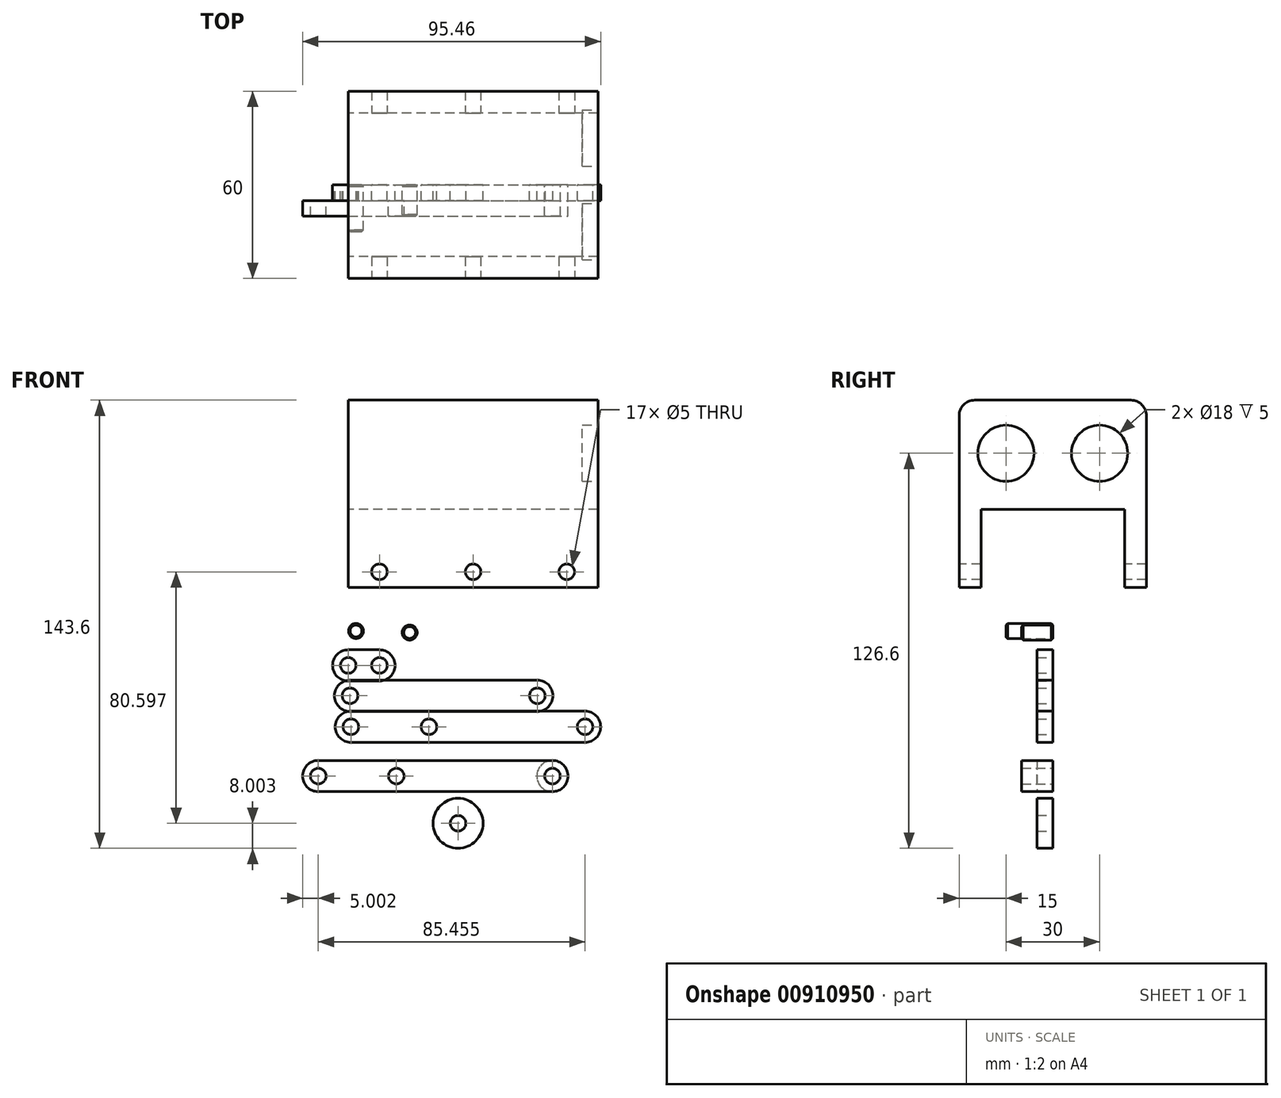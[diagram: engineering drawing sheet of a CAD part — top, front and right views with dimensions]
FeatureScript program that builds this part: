
annotation { "Feature Type Name" : "Feature", "Feature Type Description" : "" }
export const myFeature = defineFeature(function(context is Context, id is Id, definition is map)
    precondition{}
    {
        {
            assignVariable(context, id + "F0", {"name" : "thickness", "anyValue" : 5});
        }
        {
            var Q0;
            Q0=qCreatedBy(makeId("Front.planeOp"),FACE);
            var sketch = newSketch(context, id + "F1", { "sketchPlane" : qUnion([Q0])});
            skArc(sketch, "E0", {"start": v(0, 5) * mm, "mid": v(-5, 0) * mm, "end": v(0, -5) * mm});
            skArc(sketch, "E1", {"start": v(10, -5) * mm, "mid": v(15, 0) * mm, "end": v(10, 5) * mm});
            skLineSegment(sketch, "E2", {"start": v(0, 5) * mm, "end": v(10, 5) * mm});
            skLineSegment(sketch, "E3", {"start": v(0, -5) * mm, "end": v(10, -5) * mm});
            skCircle(sketch, "E4", {"center": v(0, 0) * mm, "radius": 2.5 * mm});
            skCircle(sketch, "E5", {"center": v(10, 0) * mm, "radius": 2.5 * mm});
            skSolve(sketch);
        }
        {
            var Q0;
            Q0=makeQuery(id+"F1.imprint","IMPRINT",FACE,{"disambiguationData":[TD([[makeQuery(id+"F1.imprint","IMPRINT",EDGE,{"derivedFrom":sQuery(id+"F1.wireOp",EDGE,"E0")}),1.0]])]});
            extrude(context, id + "F2", {"entities" : qUnion([Q0]), "depth" : (getVariable(context, 'thickness')) * mm, "offsetDistance" : 25 * mm});
        }
        {
            var Q0;
            Q0=qCreatedBy(makeId("Front.planeOp"),FACE);
            var sketch = newSketch(context, id + "F3", { "sketchPlane" : qUnion([Q0])});
            skArc(sketch, "E6", {"start": v(0.57, -4.73) * mm, "mid": v(-4.43, -9.73) * mm, "end": v(0.57, -14.73) * mm});
            skArc(sketch, "E7", {"start": v(60.57, -14.73) * mm, "mid": v(65.57, -9.73) * mm, "end": v(60.57, -4.73) * mm});
            skLineSegment(sketch, "E8", {"start": v(0.57, -4.73) * mm, "end": v(60.57, -4.73) * mm});
            skLineSegment(sketch, "E9", {"start": v(0.57, -14.73) * mm, "end": v(60.57, -14.73) * mm});
            skCircle(sketch, "E10", {"center": v(0.57, -9.73) * mm, "radius": 2.5 * mm});
            skCircle(sketch, "E11", {"center": v(60.57, -9.73) * mm, "radius": 2.5 * mm});
            skSolve(sketch);
        }
        {
            var Q0;
            Q0=makeQuery(id+"F3.imprint","IMPRINT",FACE,{"disambiguationData":[TD([[makeQuery(id+"F3.imprint","IMPRINT",EDGE,{"derivedFrom":sQuery(id+"F3.wireOp",EDGE,"E6")}),1.0]])]});
            extrude(context, id + "F4", {"entities" : qUnion([Q0]), "depth" : (getVariable(context, 'thickness')) * mm, "offsetDistance" : 25 * mm});
        }
        {
            var Q0;
            Q0=qCreatedBy(makeId("Front.planeOp"),FACE);
            var sketch = newSketch(context, id + "F5", { "sketchPlane" : qUnion([Q0])});
            skArc(sketch, "E12", {"start": v(0.86, -14.66) * mm, "mid": v(-4.14, -19.66) * mm, "end": v(0.86, -24.66) * mm});
            skArc(sketch, "E13", {"start": v(75.86, -24.66) * mm, "mid": v(80.86, -19.66) * mm, "end": v(75.86, -14.66) * mm});
            skLineSegment(sketch, "E14", {"start": v(0.86, -14.66) * mm, "end": v(75.86, -14.66) * mm});
            skLineSegment(sketch, "E15", {"start": v(0.86, -24.66) * mm, "end": v(75.86, -24.66) * mm});
            skCircle(sketch, "E16", {"center": v(0.86, -19.66) * mm, "radius": 2.5 * mm});
            skCircle(sketch, "E17", {"center": v(75.86, -19.66) * mm, "radius": 2.5 * mm});
            skCircle(sketch, "E18", {"center": v(25.86, -19.66) * mm, "radius": 2.5 * mm});
            skSolve(sketch);
        }
        {
            var Q0;
            Q0=makeQuery(id+"F5.imprint","IMPRINT",FACE,{"disambiguationData":[TD([[makeQuery(id+"F5.imprint","IMPRINT",EDGE,{"derivedFrom":sQuery(id+"F5.wireOp",EDGE,"E12")}),1.0]])]});
            extrude(context, id + "F6", {"entities" : qUnion([Q0]), "depth" : (getVariable(context, 'thickness')) * mm, "offsetDistance" : 25 * mm});
        }
        {
            var Q0;
            Q0=qCreatedBy(makeId("Top.planeOp"),FACE);
            cPlane(context, id + "F7", {"entities" : qUnion([Q0]), "cplaneType" : CPlaneType.OFFSET, "offset" : 25 * mm, "width" : 150 * mm, "height" : 150 * mm});
        }
        {
            var Q0;
            Q0=qCreatedBy(id+"F7.planeOp",FACE);
            var sketch = newSketch(context, id + "F8", { "sketchPlane" : qUnion([Q0])});
            skLineSegment(sketch, "E19.bottom", {"start": v(0, 30) * mm, "end": v(80, 30) * mm});
            skLineSegment(sketch, "E19.top", {"start": v(0, -30) * mm, "end": v(80, -30) * mm});
            skLineSegment(sketch, "E19.left", {"start": v(0, 30) * mm, "end": v(0, -30) * mm});
            skLineSegment(sketch, "E19.right", {"start": v(80, 30) * mm, "end": v(80, -30) * mm});
            skSolve(sketch);
        }
        {
            var Q0;
            Q0=makeQuery(id+"F8.imprint","IMPRINT",FACE,{"disambiguationData":[TD([[makeQuery(id+"F8.imprint","IMPRINT",EDGE,{"derivedFrom":sQuery(id+"F8.wireOp",EDGE,"E19.bottom")}),-1.0]])]});
            extrude(context, id + "F9", {"entities" : qUnion([Q0]), "depth" : 60 * mm, "offsetDistance" : 25 * mm});
        }
        {
            var Q0;
            Q0=makeQuery(id+"F9.opExtrude","SWEPT_FACE",FACE,{"disambiguationData":[OSD([sQuery(id+"F8.wireOp",EDGE,"E19.top")])]});
            var sketch = newSketch(context, id + "F10", { "sketchPlane" : qUnion([Q0])});
            skCircle(sketch, "E20", {"center": v(10, 30) * mm, "radius": 2.5 * mm});
            skCircle(sketch, "E21", {"center": v(70, 30) * mm, "radius": 2.5 * mm});
            skCircle(sketch, "E22", {"center": v(40, 30) * mm, "radius": 2.5 * mm});
            skPoint(sketch, "E22.centerSnap0", {"position": v(40, 25) * mm});
            skSolve(sketch);
        }
        {
            var Q0;
            Q0=qSketchRegion(id+"F10",true);
            extrude(context, id + "F11", {"entities" : qUnion([Q0]), "operationType" : NewBodyOperationType.REMOVE, "endBound" : BoundingType.THROUGH_ALL, "oppositeDirection" : true, "depth" : 25 * mm, "offsetDistance" : 25 * mm});
        }
        {
            var Q0;
            Q0=qCreatedBy(makeId("Front.planeOp"),FACE);
            var sketch = newSketch(context, id + "F12", { "sketchPlane" : qUnion([Q0])});
            skCircle(sketch, "E23", {"center": v(2.49, 11.02) * mm, "radius": 2.4 * mm});
            skSolve(sketch);
        }
        {
            var Q0;
            Q0=makeQuery(id+"F12.imprint","IMPRINT",FACE,{"disambiguationData":[TD([[makeQuery(id+"F12.imprint","IMPRINT",EDGE,{"derivedFrom":sQuery(id+"F12.wireOp",EDGE,"E23")}),1.0]])]});
            extrude(context, id + "F13", {"entities" : qUnion([Q0]), "depth" : 15 * mm, "offsetDistance" : 25 * mm});
        }
        {
            var Q0;
            Q0=qCreatedBy(makeId("Front.planeOp"),FACE);
            var sketch = newSketch(context, id + "F14", { "sketchPlane" : qUnion([Q0])});
            skCircle(sketch, "E24", {"center": v(35.18, -50.6) * mm, "radius": 2.5 * mm});
            skCircle(sketch, "E25", {"center": v(35.18, -50.6) * mm, "radius": 8 * mm});
            skSolve(sketch);
        }
        {
            var Q0;
            Q0=makeQuery(id+"F14.imprint","IMPRINT",FACE,{"disambiguationData":[TD([[makeQuery(id+"F14.imprint","IMPRINT",EDGE,{"derivedFrom":sQuery(id+"F14.wireOp",EDGE,"E24")}),-1.0]])]});
            extrude(context, id + "F15", {"entities" : qUnion([Q0]), "depth" : 5 * mm, "offsetDistance" : 25 * mm});
        }
        {
            var Q0;
            Q0=qCreatedBy(makeId("Front.planeOp"),FACE);
            var sketch = newSketch(context, id + "F16", { "sketchPlane" : qUnion([Q0])});
            skArc(sketch, "E26", {"start": v(-9.6, -30.46) * mm, "mid": v(-14.6, -35.46) * mm, "end": v(-9.6, -40.46) * mm});
            skArc(sketch, "E27", {"start": v(65.4, -40.46) * mm, "mid": v(70.4, -35.46) * mm, "end": v(65.4, -30.46) * mm});
            skLineSegment(sketch, "E28", {"start": v(-9.6, -30.46) * mm, "end": v(65.4, -30.46) * mm});
            skLineSegment(sketch, "E29", {"start": v(-9.6, -40.46) * mm, "end": v(65.4, -40.46) * mm});
            skCircle(sketch, "E30", {"center": v(-9.6, -35.46) * mm, "radius": 2.5 * mm});
            skCircle(sketch, "E31", {"center": v(65.4, -35.46) * mm, "radius": 2.5 * mm});
            skCircle(sketch, "E32", {"center": v(15.4, -35.46) * mm, "radius": 2.5 * mm});
            skSolve(sketch);
        }
        {
            var Q0;
            Q0=makeQuery(id+"F16.imprint","IMPRINT",FACE,{"disambiguationData":[TD([[makeQuery(id+"F16.imprint","IMPRINT",EDGE,{"derivedFrom":sQuery(id+"F16.wireOp",EDGE,"E26")}),1.0]])]});
            extrude(context, id + "F17", {"entities" : qUnion([Q0]), "depth" : (getVariable(context, 'thickness')) * mm * 2, "offsetDistance" : 25 * mm});
        }
        {
            var Q0;
            Q0=makeQuery(id+"F17.opExtrude","CAP_FACE",FACE,{"disambiguationData":[OSD([sQuery(id+"F16.wireOp",EDGE,"E26"),sQuery(id+"F16.wireOp",EDGE,"E27"),sQuery(id+"F16.wireOp",EDGE,"E28"),sQuery(id+"F16.wireOp",EDGE,"E29"),sQuery(id+"F16.wireOp",EDGE,"E30"),sQuery(id+"F16.wireOp",EDGE,"E31"),sQuery(id+"F16.wireOp",EDGE,"E32")])],"isStart":true});
            var sketch = newSketch(context, id + "F18", { "sketchPlane" : qUnion([Q0])});
            skLineSegment(sketch, "E33", {"start": v(9.6, -30.46) * mm, "end": v(-65.4, -30.46) * mm});
            skLineSegment(sketch, "E34", {"start": v(9.6, -40.46) * mm, "end": v(-65.4, -40.46) * mm});
            skArc(sketch, "E35", {"start": v(9.6, -40.46) * mm, "mid": v(14.6, -35.46) * mm, "end": v(9.6, -30.46) * mm});
            skArc(sketch, "E36", {"start": v(-65.4, -40.46) * mm, "mid": v(-60.4, -35.46) * mm, "end": v(-65.4, -30.46) * mm});
            skSolve(sketch);
        }
        {
            var Q0;
            Q0=makeQuery(id+"F18.imprint","IMPRINT",FACE,{"disambiguationData":[TD([[makeQuery(id+"F18.imprint","IMPRINT",EDGE,{"derivedFrom":sQuery(id+"F18.wireOp",EDGE,"E33")}),1.0]])]});
            extrude(context, id + "F19", {"entities" : qUnion([Q0]), "operationType" : NewBodyOperationType.REMOVE, "oppositeDirection" : true, "depth" : 5 * mm, "offsetDistance" : 25 * mm});
        }
        {
            var Q0;
            Q0=qCreatedBy(makeId("Front.planeOp"),FACE);
            var sketch = newSketch(context, id + "F20", { "sketchPlane" : qUnion([Q0])});
            skCircle(sketch, "E37", {"center": v(19.67, 10.54) * mm, "radius": 2.4 * mm});
            skSolve(sketch);
        }
        {
            var Q0;
            Q0=makeQuery(id+"F20.imprint","IMPRINT",FACE,{"disambiguationData":[TD([[makeQuery(id+"F20.imprint","IMPRINT",EDGE,{"derivedFrom":sQuery(id+"F20.wireOp",EDGE,"E37")}),1.0]])]});
            extrude(context, id + "F21", {"entities" : qUnion([Q0]), "depth" : 10 * mm, "offsetDistance" : 25 * mm});
        }
        {
            var Q0;
            Q0=makeQuery(id+"F9.opExtrude","CAP_FACE",FACE,{"disambiguationData":[OSD([sQuery(id+"F8.wireOp",EDGE,"E19.bottom"),sQuery(id+"F8.wireOp",EDGE,"E19.top"),sQuery(id+"F8.wireOp",EDGE,"E19.left"),sQuery(id+"F8.wireOp",EDGE,"E19.right")])],"isStart":true});
            var sketch = newSketch(context, id + "F22", { "sketchPlane" : qUnion([Q0])});
            skLineSegment(sketch, "E38.bottom", {"start": v(73, -23) * mm, "end": v(7, -23) * mm});
            skLineSegment(sketch, "E38.top", {"start": v(73, 23) * mm, "end": v(7, 23) * mm});
            skLineSegment(sketch, "E38.left", {"start": v(73, -23) * mm, "end": v(73, 23) * mm});
            skLineSegment(sketch, "E38.right", {"start": v(7, -23) * mm, "end": v(7, 23) * mm});
            skPoint(sketch, "E38.middle", {"position": v(40, 0) * mm});
            skSolve(sketch);
        }
        {
            var Q0;
            Q0=makeQuery(id+"F22.imprint","IMPRINT",FACE,{"disambiguationData":[TD([[makeQuery(id+"F22.imprint","IMPRINT",EDGE,{"derivedFrom":sQuery(id+"F22.wireOp",EDGE,"E38.bottom")}),-1.0]])]});
            extrude(context, id + "F23", {"entities" : qUnion([Q0]), "operationType" : NewBodyOperationType.REMOVE, "oppositeDirection" : true, "depth" : 25 * mm, "offsetDistance" : 25 * mm});
        }
        {
            var Q0;
            Q0=makeQuery(id+"F9.opExtrude","SWEPT_FACE",FACE,{"disambiguationData":[OSD([sQuery(id+"F8.wireOp",EDGE,"E19.right")])]});
            var sketch = newSketch(context, id + "F24", { "sketchPlane" : qUnion([Q0])});
            skLineSegment(sketch, "E39.bottom", {"start": v(-23, 25) * mm, "end": v(23, 25) * mm});
            skLineSegment(sketch, "E39.top", {"start": v(-23, 50) * mm, "end": v(23, 50) * mm});
            skLineSegment(sketch, "E39.left", {"start": v(-23, 25) * mm, "end": v(-23, 50) * mm});
            skLineSegment(sketch, "E39.right", {"start": v(23, 25) * mm, "end": v(23, 50) * mm});
            skSolve(sketch);
        }
        {
            var Q0;
            Q0=makeQuery(id+"F24.imprint","IMPRINT",FACE,{"disambiguationData":[TD([[makeQuery(id+"F24.imprint","IMPRINT",EDGE,{"derivedFrom":sQuery(id+"F24.wireOp",EDGE,"E39.bottom")}),-1.0]])]});
            extrude(context, id + "F25", {"entities" : qUnion([Q0]), "operationType" : NewBodyOperationType.REMOVE, "endBound" : BoundingType.THROUGH_ALL, "oppositeDirection" : true, "depth" : 25 * mm, "offsetDistance" : 25 * mm});
        }
        {
            var Q0;
            Q0=makeQuery(id+"F9.opExtrude","SWEPT_FACE",FACE,{"disambiguationData":[OSD([sQuery(id+"F8.wireOp",EDGE,"E19.right")])]});
            var sketch = newSketch(context, id + "F26", { "sketchPlane" : qUnion([Q0])});
            skCircle(sketch, "E40", {"center": v(-15, 68) * mm, "radius": 9 * mm});
            skCircle(sketch, "E41.MirrorC", {"center": v(15, 68) * mm, "radius": 9 * mm});
            skSolve(sketch);
        }
        {
            var Q0;
            Q0 = qSketchRegion(id + "F26", true);
            extrude(context, id + "F27", {"entities" : qUnion([Q0]), "operationType" : NewBodyOperationType.REMOVE, "oppositeDirection" : true, "depth" : 5 * mm, "offsetDistance" : 25 * mm});
        }
        {
            var Q0;
            Q0=makeQuery(id+"F9.opExtrude","CAP_EDGE",EDGE,{"disambiguationData":[OSD([sQuery(id+"F8.wireOp",EDGE,"E19.bottom")])],"isStart":false});
            var Q1;
            Q1=makeQuery(id+"F9.opExtrude","CAP_EDGE",EDGE,{"disambiguationData":[OSD([sQuery(id+"F8.wireOp",EDGE,"E19.top")])],"isStart":false});
            fillet(context, id + "F28", {"entities" : qUnion([Q0, Q1]), "radius" : 5 * mm, "tangentPropagation" : true, "allowEdgeOverflow" : false});
        }
        {
            var Q0;
            Q0=makeQuery(id+"F13.opExtrude","CAP_EDGE",EDGE,{"disambiguationData":[OSD([sQuery(id+"F12.wireOp",EDGE,"E23")])],"isStart":false});
            var Q1;
            Q1=makeQuery(id+"F21.opExtrude","CAP_EDGE",EDGE,{"disambiguationData":[OSD([sQuery(id+"F20.wireOp",EDGE,"E37")])],"isStart":false});
            var Q2;
            Q2=makeQuery(id+"F13.opExtrude","CAP_EDGE",EDGE,{"disambiguationData":[OSD([sQuery(id+"F12.wireOp",EDGE,"E23")])],"isStart":true});
            var Q3;
            Q3=makeQuery(id+"F21.opExtrude","CAP_EDGE",EDGE,{"disambiguationData":[OSD([sQuery(id+"F20.wireOp",EDGE,"E37")])],"isStart":true});
            chamfer(context, id + "F29", {"entities" : qUnion([Q0, Q1, Q2, Q3]), "width" : 0.5 * mm, "tangentPropagation" : true});
        }
    });
